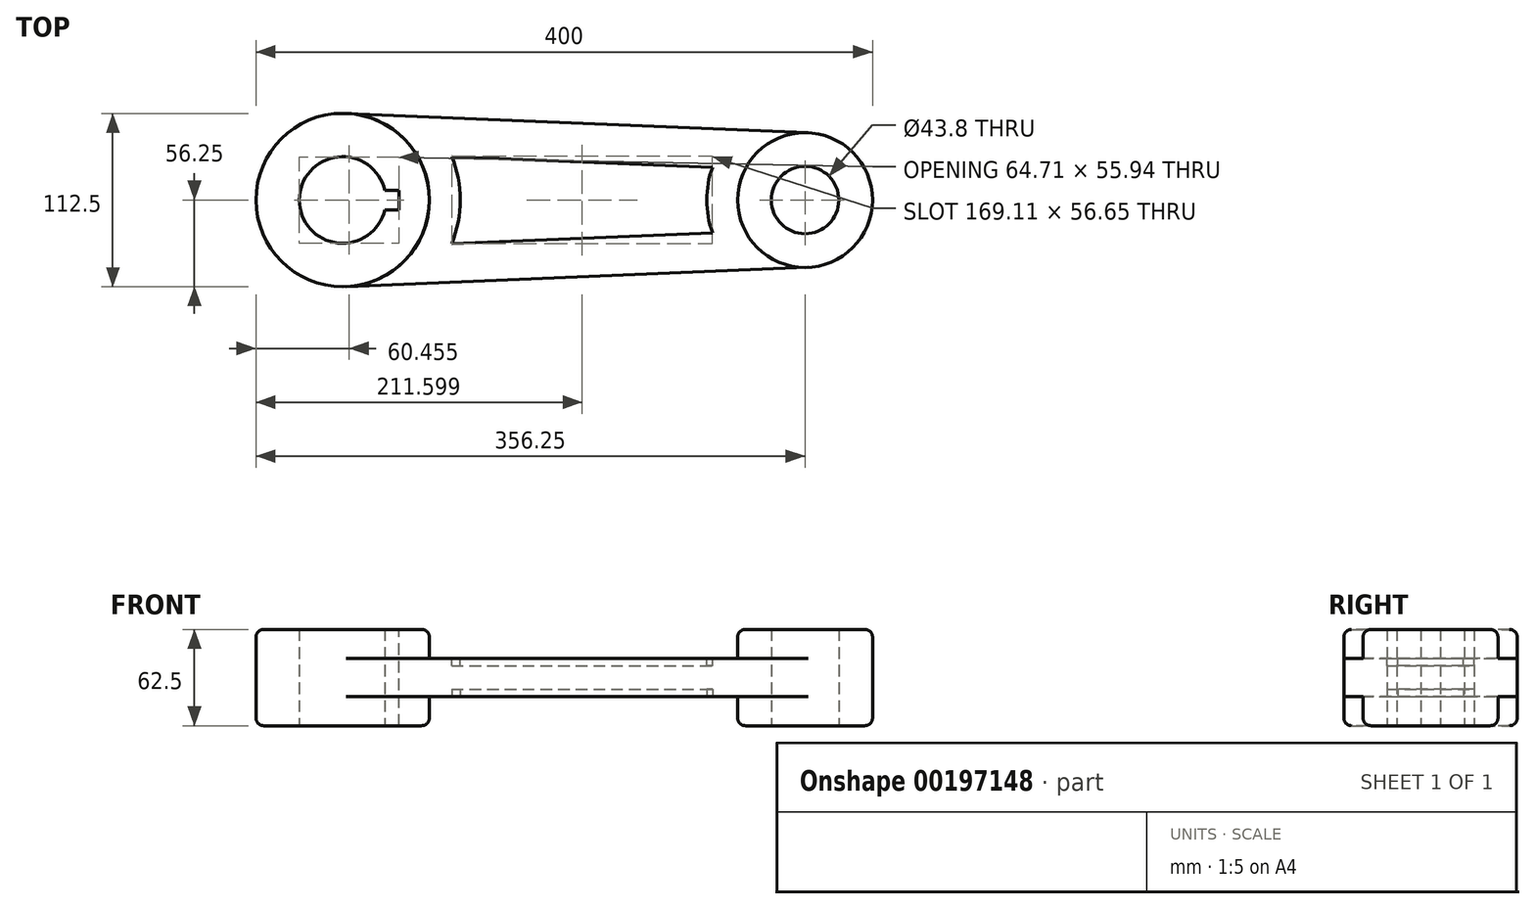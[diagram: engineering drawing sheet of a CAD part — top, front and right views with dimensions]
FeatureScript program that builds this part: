
annotation { "Feature Type Name" : "Feature", "Feature Type Description" : "" }
export const myFeature = defineFeature(function(context is Context, id is Id, definition is map)
    precondition{}
    {
        {
            var Q0;
            Q0=qCreatedBy(makeId("Top.planeOp"),FACE);
            var sketch = newSketch(context, id + "F0", { "sketchPlane" : qUnion([Q0])});
            skCircle(sketch, "E0", {"center": v(-80.9, 0) * mm, "radius": 56.25 * mm});
            skCircle(sketch, "E1", {"center": v(-80.9, 0) * mm, "radius": 28.15 * mm});
            skCircle(sketch, "E2", {"center": v(219.1, 0) * mm, "radius": 43.75 * mm});
            skCircle(sketch, "E3", {"center": v(219.1, 0) * mm, "radius": 21.9 * mm});
            skLineSegment(sketch, "E4", {"start": v(-78.55, 56.2) * mm, "end": v(220.93, 43.71) * mm});
            skLineSegment(sketch, "E5", {"start": v(-78.55, -56.2) * mm, "end": v(220.93, -43.71) * mm});
            skSolve(sketch);
        }
        {
            var Q0;
            {var subQ0=sQuery(id+"F0.wireOp",EDGE,"E4");Q0=makeQuery(id+"F0.imprint","IMPRINT",FACE,{"disambiguationData":[TD([[makeQuery(id+"F0.imprint","IMPRINT",EDGE,{"derivedFrom":subQ0}),-1.0]])]});}
            extrude(context, id + "F6", {"entities" : qUnion([Q0]), "depth" : 12.5 * mm});
        }
        {
            var Q0;
            Q0=makeQuery(id+"F0.imprint","IMPRINT",FACE,{"disambiguationData":[TD([[makeQuery(id+"F0.imprint","IMPRINT",EDGE,{"derivedFrom":sQuery(id+"F0.wireOp",EDGE,"E3")}),-1.0]])]});
            var Q1;
            Q1=makeQuery(id+"F0.imprint","IMPRINT",FACE,{"disambiguationData":[TD([[makeQuery(id+"F0.imprint","IMPRINT",EDGE,{"derivedFrom":sQuery(id+"F0.wireOp",EDGE,"E1")}),-1.0]])]});
            extrude(context, id + "F1", {"entities" : qUnion([Q0, Q1]), "operationType" : NewBodyOperationType.ADD, "depth" : 31.25 * mm});
        }
        {
            var Q0;
            Q0=makeQuery(id+"F6.opExtrude","CAP_FACE",FACE,{"disambiguationData":[OSD([sQuery(id+"F0.wireOp",EDGE,"E0"),sQuery(id+"F0.wireOp",EDGE,"E2"),sQuery(id+"F0.wireOp",EDGE,"E4"),sQuery(id+"F0.wireOp",EDGE,"E5")])],"isStart":false});
            var sketch = newSketch(context, id + "F7", { "sketchPlane" : qUnion([Q0])});
            skArc(sketch, "E6", {"start": v(159.01, 21.27) * mm, "mid": v(155.36, 0) * mm, "end": v(159.01, -21.27) * mm});
            skArc(sketch, "E7", {"start": v(-10.1, -28.32) * mm, "mid": v(-4.64, 0) * mm, "end": v(-10.1, 28.32) * mm});
            skLineSegment(sketch, "E8.0", {"start": v(-10.1, 28.32) * mm, "end": v(159.01, 21.27) * mm});
            skLineSegment(sketch, "E9.0", {"start": v(-10.1, -28.32) * mm, "end": v(159.01, -21.27) * mm});
            skSolve(sketch);
        }
        {
            var Q0;
            Q0 = qSketchRegion(id + "F7", true);
            extrude(context, id + "F2", {"entities" : qUnion([Q0]), "operationType" : NewBodyOperationType.REMOVE, "oppositeDirection" : true, "depth" : 5 * mm});
        }
        {
            var Q0;
            Q0=makeQuery(id+"F1.opExtrude","CAP_FACE",FACE,{"disambiguationData":[OSD([sQuery(id+"F0.wireOp",EDGE,"E0"),sQuery(id+"F0.wireOp",EDGE,"E1")])],"isStart":false});
            var sketch = newSketch(context, id + "F3", { "sketchPlane" : qUnion([Q0])});
            skLineSegment(sketch, "E10.top", {"start": v(-80.9, 6.3) * mm, "end": v(-44.33, 6.3) * mm});
            skLineSegment(sketch, "E10.left", {"start": v(-80.9, 0) * mm, "end": v(-80.9, 6.3) * mm});
            skLineSegment(sketch, "E10.right", {"start": v(-44.33, 0) * mm, "end": v(-44.33, 6.3) * mm});
            skLineSegment(sketch, "E11.MirrorCS", {"start": v(-44.33, 12.6) * mm, "end": v(-44.33, 6.3) * mm});
            skLineSegment(sketch, "E12.MirrorCS", {"start": v(-80.9, 0) * mm, "end": v(-80.9, -6.3) * mm});
            skLineSegment(sketch, "E13.MirrorCS", {"start": v(-80.9, -6.3) * mm, "end": v(-44.33, -6.3) * mm});
            skLineSegment(sketch, "E14.MirrorCS", {"start": v(-44.33, 0) * mm, "end": v(-44.33, -6.3) * mm});
            skSolve(sketch);
        }
        {
            var Q0;
            Q0 = qSketchRegion(id + "F3", true);
            extrude(context, id + "F4", {"entities" : qUnion([Q0]), "operationType" : NewBodyOperationType.REMOVE, "oppositeDirection" : true, "depth" : 130.65 * mm});
        }
        {
            var Q0;
            Q0=makeQuery(id+"F1.opExtrude","CAP_EDGE",EDGE,{"disambiguationData":[OSD([sQuery(id+"F0.wireOp",EDGE,"E0")])],"isStart":false});
            var Q1;
            Q1=makeQuery(id+"F1.opExtrude","CAP_EDGE",EDGE,{"disambiguationData":[OSD([sQuery(id+"F0.wireOp",EDGE,"E2")])],"isStart":false});
            fillet(context, id + "F5", {"entities" : qUnion([Q0, Q1]), "radius" : 5 * mm, "tangentPropagation" : true, "allowEdgeOverflow" : false});
        }
        {
            var Q0;
            Q0=makeQuery(id+"F6.opExtrude","SWEPT_BODY",BODY,{"disambiguationData":[OSD([sQuery(id+"F0.wireOp",EDGE,"E0"),sQuery(id+"F0.wireOp",EDGE,"E2"),sQuery(id+"F0.wireOp",EDGE,"E4"),sQuery(id+"F0.wireOp",EDGE,"E5")])]});
            var Q1;
            {var subQ0=sQuery(id+"F0.wireOp",EDGE,"E4");Q1=makeQuery(id+"F0.imprint","IMPRINT",FACE,{"disambiguationData":[TD([[makeQuery(id+"F0.imprint","IMPRINT",EDGE,{"derivedFrom":subQ0}),-1.0]])]});}
            mirror(context, id + "F8", {"operationType" : NewBodyOperationType.ADD, "entities" : qUnion([Q0]), "mirrorPlane" : qUnion([Q1])});
        }
    });
